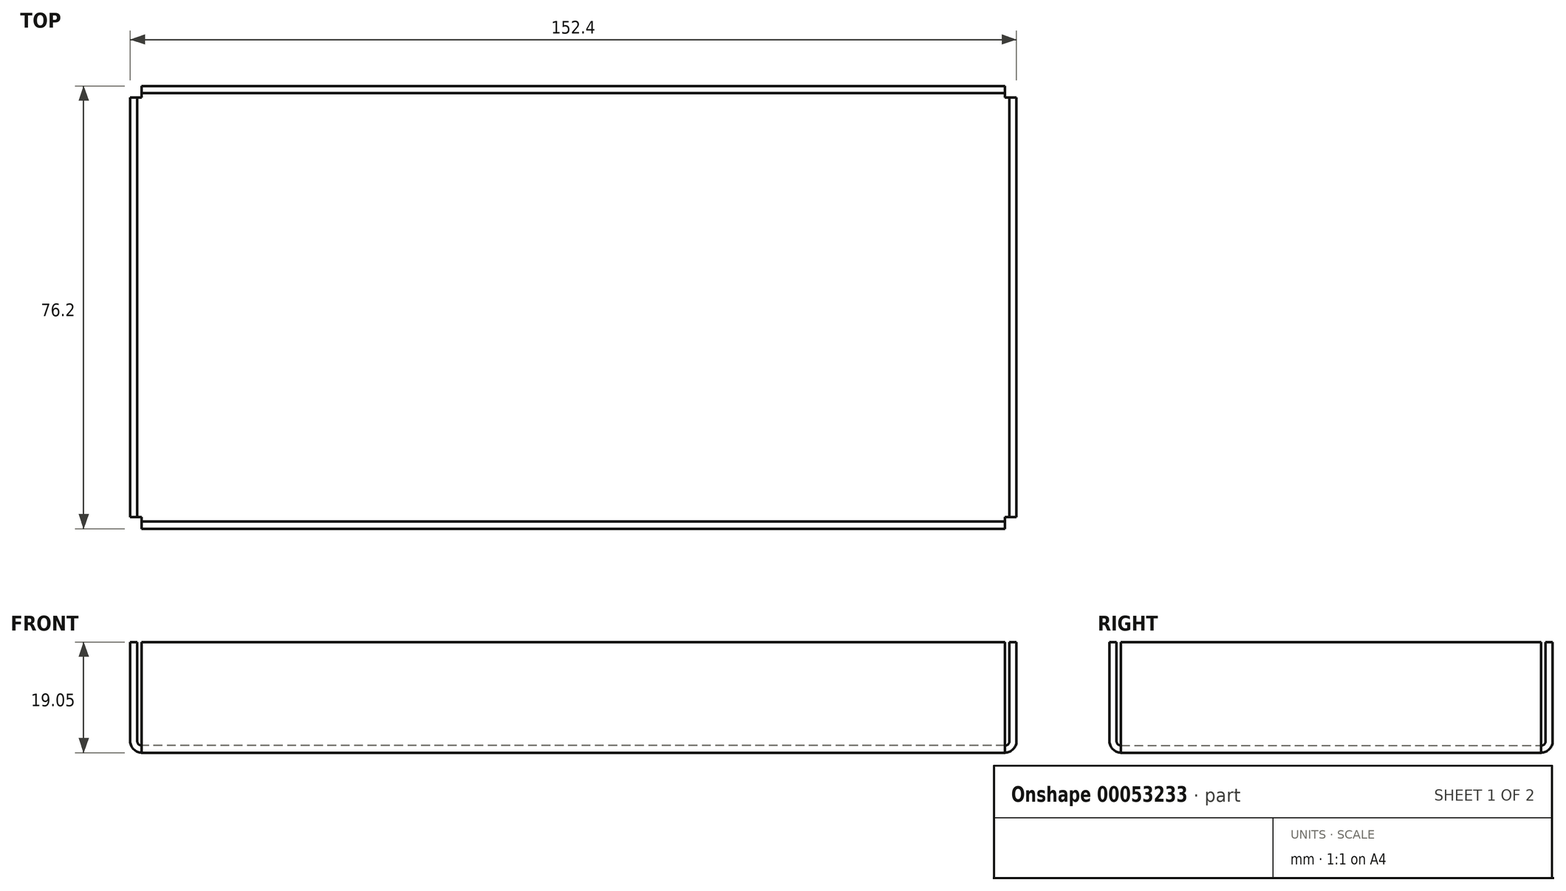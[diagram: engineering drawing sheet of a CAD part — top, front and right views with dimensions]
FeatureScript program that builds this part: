
annotation { "Feature Type Name" : "Feature", "Feature Type Description" : "" }
export const myFeature = defineFeature(function(context is Context, id is Id, definition is map)
    precondition{}
    {
        {
            var Q0;
            Q0=qCreatedBy(makeId("Top.planeOp"),FACE);
            var sketch = newSketch(context, id + "F0", { "sketchPlane" : qUnion([Q0])});
            skLineSegment(sketch, "E0.rect.bottom", {"start": v(76.2, -38.1) * mm, "end": v(-76.2, -38.1) * mm});
            skLineSegment(sketch, "E0.rect.top", {"start": v(76.2, 38.1) * mm, "end": v(-76.2, 38.1) * mm});
            skLineSegment(sketch, "E0.rect.left", {"start": v(76.2, -38.1) * mm, "end": v(76.2, 38.1) * mm});
            skLineSegment(sketch, "E0.rect.right", {"start": v(-76.2, -38.1) * mm, "end": v(-76.2, 38.1) * mm});
            skPoint(sketch, "E0.rect.middle", {"position": v(0, 0) * mm});
            skSolve(sketch);
        }
        {
            var Q0;
            Q0=makeQuery(id+"F0.imprint","IMPRINT",FACE,{"disambiguationData":[TD([[makeQuery(id+"F0.imprint","IMPRINT",EDGE,{"derivedFrom":sQuery(id+"F0.wireOp",EDGE,"E0.rect.bottom")}),-1.0]])]});
            extrude(context, id + "F1", {"entities" : qUnion([Q0]), "depth" : 19.05 * mm});
        }
        {
            var Q0;
            Q0=makeQuery(id+"F1.opExtrude","CAP_FACE",FACE,{"disambiguationData":[OSD([sQuery(id+"F0.wireOp",EDGE,"E0.rect.bottom"),sQuery(id+"F0.wireOp",EDGE,"E0.rect.top"),sQuery(id+"F0.wireOp",EDGE,"E0.rect.left"),sQuery(id+"F0.wireOp",EDGE,"E0.rect.right")])],"isStart":false});
            shell(context, id + "F2", {"entities" : qUnion([Q0]), "thickness" : 1.21 * mm});
        }
        {
            var Q0;
            Q0=makeQuery(id+"F1.opExtrude","CAP_FACE",FACE,{"disambiguationData":[OSD([sQuery(id+"F0.wireOp",EDGE,"E0.rect.bottom"),sQuery(id+"F0.wireOp",EDGE,"E0.rect.top"),sQuery(id+"F0.wireOp",EDGE,"E0.rect.left"),sQuery(id+"F0.wireOp",EDGE,"E0.rect.right")])],"isStart":false});
            var sketch = newSketch(context, id + "F3", { "sketchPlane" : qUnion([Q0])});
            skLineSegment(sketch, "E1.bottom", {"start": v(-76.2, -38.1) * mm, "end": v(-74.22, -38.1) * mm});
            skLineSegment(sketch, "E1.top", {"start": v(-76.2, -36.12) * mm, "end": v(-74.22, -36.12) * mm});
            skLineSegment(sketch, "E1.left", {"start": v(-76.2, -38.1) * mm, "end": v(-76.2, -36.12) * mm});
            skLineSegment(sketch, "E1.right", {"start": v(-74.22, -38.1) * mm, "end": v(-74.22, -36.12) * mm});
            skLineSegment(sketch, "E2.MirrorCS", {"start": v(-76.2, 38.1) * mm, "end": v(-74.22, 38.1) * mm});
            skLineSegment(sketch, "E3.MirrorCS", {"start": v(-76.2, 38.1) * mm, "end": v(-76.2, 36.12) * mm});
            skLineSegment(sketch, "E4.MirrorCS", {"start": v(-76.2, 36.12) * mm, "end": v(-74.22, 36.12) * mm});
            skLineSegment(sketch, "E5.MirrorCS", {"start": v(-74.22, 38.1) * mm, "end": v(-74.22, 36.12) * mm});
            skLineSegment(sketch, "E6.MirrorCS", {"start": v(76.2, -36.12) * mm, "end": v(74.22, -36.12) * mm});
            skLineSegment(sketch, "E7.MirrorCS", {"start": v(76.2, -38.1) * mm, "end": v(74.22, -38.1) * mm});
            skLineSegment(sketch, "E8.MirrorCS", {"start": v(76.2, -38.1) * mm, "end": v(76.2, -36.12) * mm});
            skLineSegment(sketch, "E9.MirrorCS", {"start": v(74.22, -38.1) * mm, "end": v(74.22, -36.12) * mm});
            skLineSegment(sketch, "E10.MirrorCS", {"start": v(74.22, 38.1) * mm, "end": v(74.22, 36.12) * mm});
            skLineSegment(sketch, "E11.MirrorCS", {"start": v(76.2, 36.12) * mm, "end": v(74.22, 36.12) * mm});
            skLineSegment(sketch, "E12.MirrorCS", {"start": v(76.2, 38.1) * mm, "end": v(76.2, 36.12) * mm});
            skLineSegment(sketch, "E13.MirrorCS", {"start": v(76.2, 38.1) * mm, "end": v(74.22, 38.1) * mm});
            skSolve(sketch);
        }
        {
            var Q0;
            Q0 = qSketchRegion(id + "F3", true);
            extrude(context, id + "F4", {"entities" : qUnion([Q0]), "operationType" : NewBodyOperationType.REMOVE, "endBound" : BoundingType.THROUGH_ALL, "oppositeDirection" : true, "depth" : 25.4 * mm});
        }
        {
            var Q0;
            {var subQ0=sQuery(id+"F0.wireOp",EDGE,"E0.rect.right");Q0=makeQuery(id+"F2.opShell","OFFSET_EDGE",EDGE,{"disambiguationData":[OSD([subQ0]),TDD([makeQuery(id+"F1.opExtrude","CAP_EDGE",EDGE,{"disambiguationData":[OSD([subQ0])],"isStart":true})])]});}
            var Q1;
            {var subQ0=sQuery(id+"F0.wireOp",EDGE,"E0.rect.top");Q1=makeQuery(id+"F2.opShell","OFFSET_EDGE",EDGE,{"disambiguationData":[OSD([subQ0]),TDD([makeQuery(id+"F1.opExtrude","CAP_EDGE",EDGE,{"disambiguationData":[OSD([subQ0])],"isStart":true})])]});}
            var Q2;
            {var subQ0=sQuery(id+"F0.wireOp",EDGE,"E0.rect.bottom");Q2=makeQuery(id+"F2.opShell","OFFSET_EDGE",EDGE,{"disambiguationData":[OSD([subQ0]),TDD([makeQuery(id+"F1.opExtrude","CAP_EDGE",EDGE,{"disambiguationData":[OSD([subQ0])],"isStart":true})])]});}
            var Q3;
            {var subQ0=sQuery(id+"F0.wireOp",EDGE,"E0.rect.left");Q3=makeQuery(id+"F2.opShell","OFFSET_EDGE",EDGE,{"disambiguationData":[OSD([subQ0]),TDD([makeQuery(id+"F1.opExtrude","CAP_EDGE",EDGE,{"disambiguationData":[OSD([subQ0])],"isStart":true})])]});}
            fillet(context, id + "F5", {"entities" : qUnion([Q0, Q1, Q2, Q3]), "radius" : 0.76 * mm, "tangentPropagation" : true, "allowEdgeOverflow" : false});
        }
        {
            var Q0;
            Q0=makeQuery(id+"F1.opExtrude","CAP_EDGE",EDGE,{"disambiguationData":[OSD([sQuery(id+"F0.wireOp",EDGE,"E0.rect.top")])],"isStart":true});
            var Q1;
            Q1=makeQuery(id+"F1.opExtrude","CAP_EDGE",EDGE,{"disambiguationData":[OSD([sQuery(id+"F0.wireOp",EDGE,"E0.rect.right")])],"isStart":true});
            var Q2;
            Q2=makeQuery(id+"F1.opExtrude","CAP_EDGE",EDGE,{"disambiguationData":[OSD([sQuery(id+"F0.wireOp",EDGE,"E0.rect.left")])],"isStart":true});
            var Q3;
            Q3=makeQuery(id+"F1.opExtrude","CAP_EDGE",EDGE,{"disambiguationData":[OSD([sQuery(id+"F0.wireOp",EDGE,"E0.rect.bottom")])],"isStart":true});
            fillet(context, id + "F6", {"entities" : qUnion([Q0, Q1, Q2, Q3]), "radius" : 1.98 * mm, "tangentPropagation" : true, "allowEdgeOverflow" : false});
        }
    });
